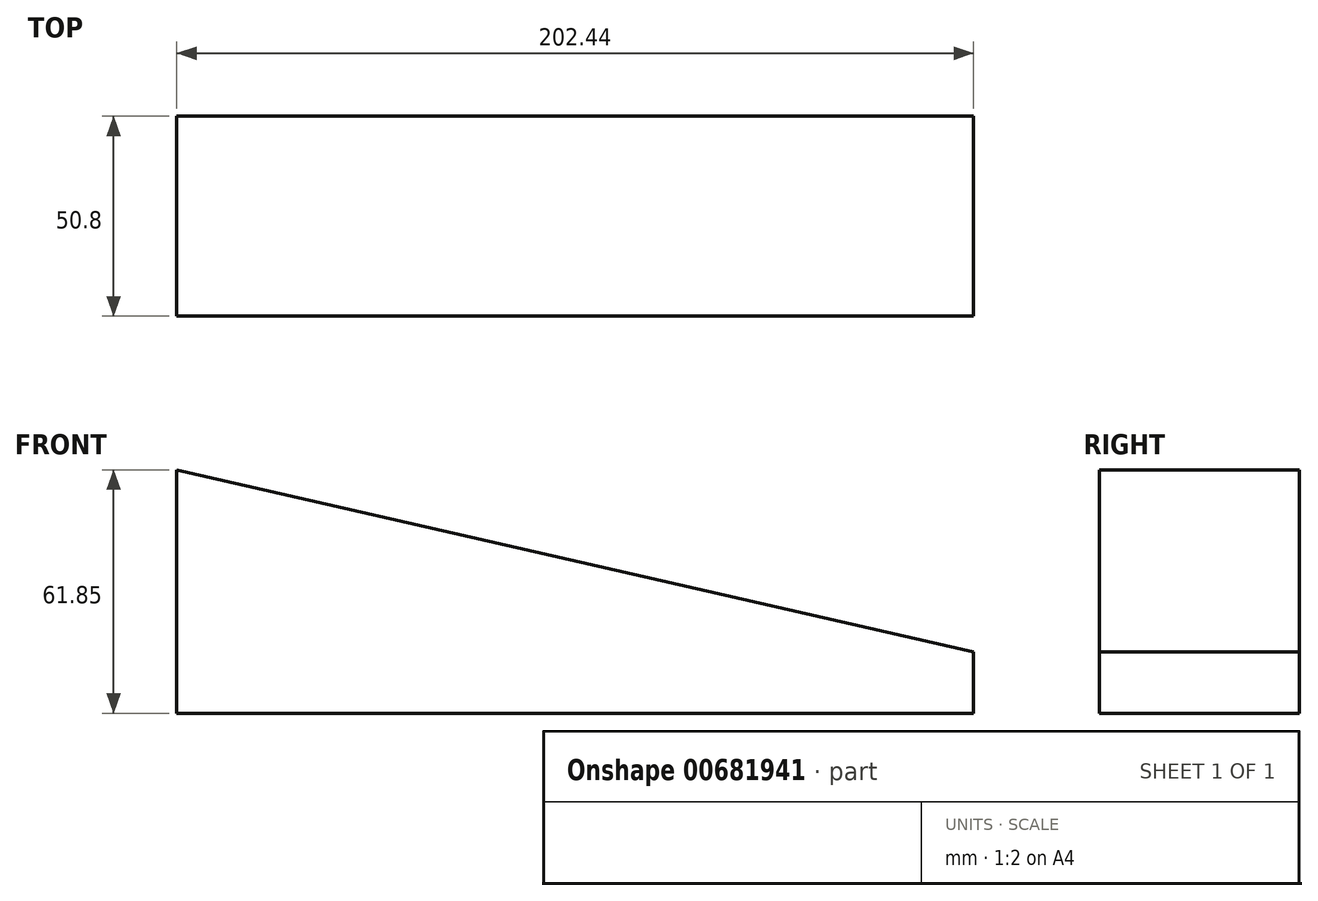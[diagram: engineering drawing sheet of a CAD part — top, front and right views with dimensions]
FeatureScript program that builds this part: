
annotation { "Feature Type Name" : "Feature", "Feature Type Description" : "" }
export const myFeature = defineFeature(function(context is Context, id is Id, definition is map)
    precondition{}
    {
        {
            var Q0;
            Q0=qCreatedBy(makeId("Front.planeOp"),FACE);
            var sketch = newSketch(context, id + "F0", { "sketchPlane" : qUnion([Q0])});
            skLineSegment(sketch, "E0", {"start": v(0, 9.78) * mm, "end": v(0, 61.85) * mm});
            skLineSegment(sketch, "E1", {"start": v(0, 61.85) * mm, "end": v(202.44, 15.62) * mm});
            skLineSegment(sketch, "E2", {"start": v(202.44, 15.62) * mm, "end": v(202.44, 0) * mm});
            skLineSegment(sketch, "E3", {"start": v(202.44, 0) * mm, "end": v(0, 0) * mm});
            skLineSegment(sketch, "E4", {"start": v(0, 0) * mm, "end": v(0, 9.78) * mm});
            skSolve(sketch);
        }
        {
            var Q0;
            Q0=makeQuery(id+"F0.imprint","IMPRINT",FACE,{"disambiguationData":[TD([[makeQuery(id+"F0.imprint","IMPRINT",EDGE,{"derivedFrom":sQuery(id+"F0.wireOp",EDGE,"E0")}),-1.0]])]});
            extrude(context, id + "F1", {"entities" : qUnion([Q0]), "oppositeDirection" : true, "depth" : 50.8 * mm, "offsetDistance" : 25.4 * mm});
        }
    });
